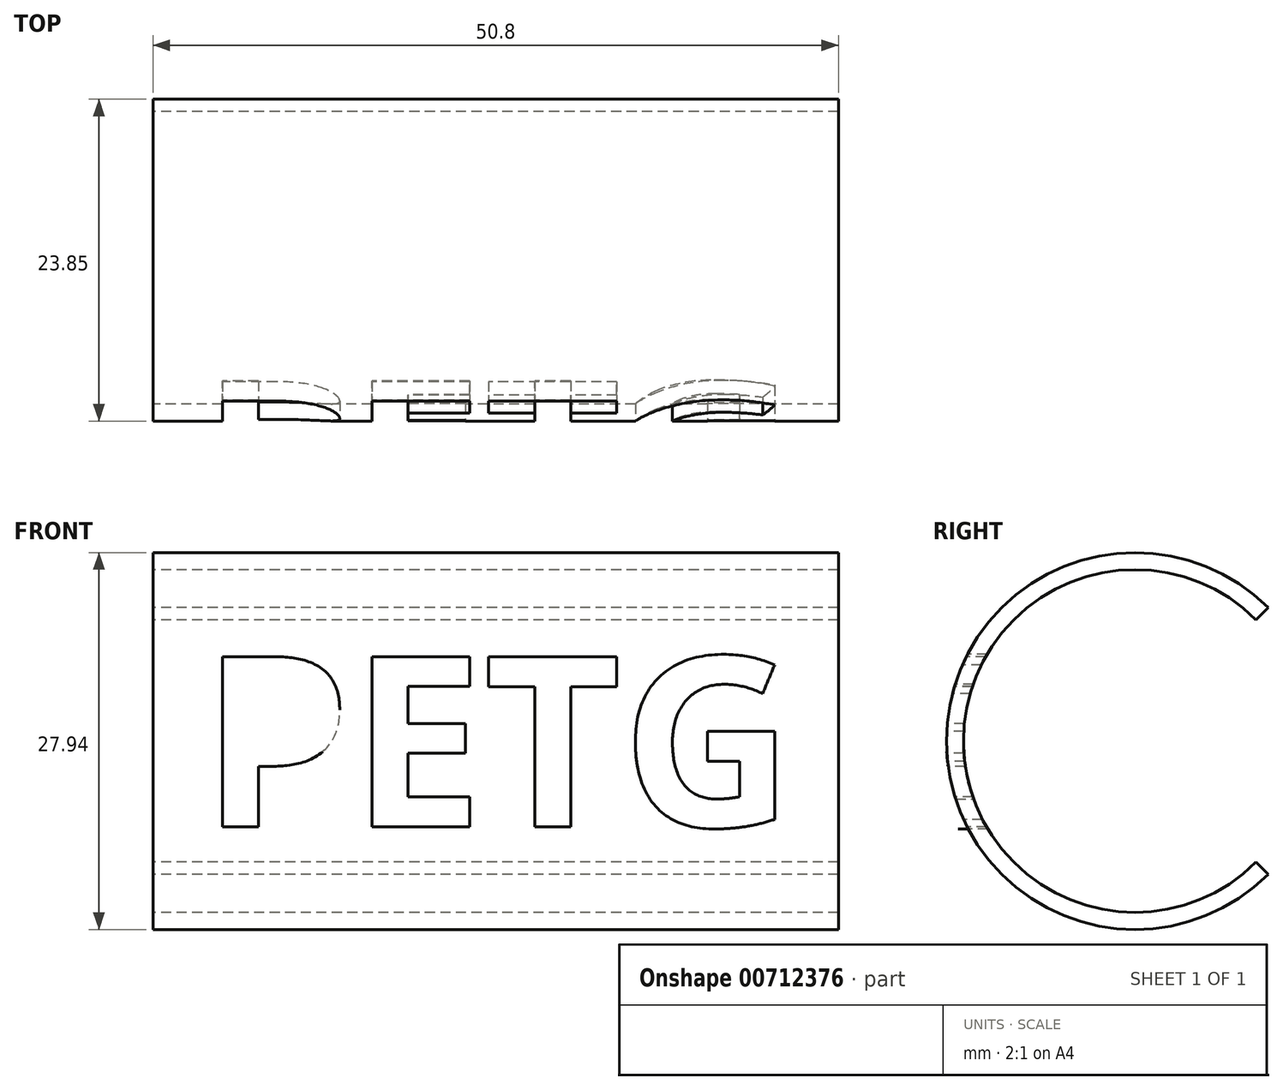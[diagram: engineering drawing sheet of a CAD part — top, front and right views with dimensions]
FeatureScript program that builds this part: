
annotation { "Feature Type Name" : "Feature", "Feature Type Description" : "" }
export const myFeature = defineFeature(function(context is Context, id is Id, definition is map)
    precondition{}
    {
        {
            var Q0;
            Q0=qCreatedBy(makeId("Right.planeOp"),FACE);
            var sketch = newSketch(context, id + "F0", { "sketchPlane" : qUnion([Q0])});
            skCircle(sketch, "E0", {"center": v(0, 0) * mm, "radius": 12.7 * mm});
            skCircle(sketch, "E1", {"center": v(0, 0) * mm, "radius": 13.97 * mm});
            skLineSegment(sketch, "E2", {"start": v(0, 0) * mm, "end": v(13.97, 0) * mm});
            skLineSegment(sketch, "E3", {"start": v(0, 0) * mm, "end": v(9.88, 9.88) * mm});
            skLineSegment(sketch, "E4.MirrorCS", {"start": v(0, 0) * mm, "end": v(9.88, -9.88) * mm});
            skSolve(sketch);
        }
        {
            var Q0;
            {var subQ0=sQuery(id+"F0.wireOp",EDGE,"E3");var subQ1=sQuery(id+"F0.wireOp",EDGE,"E0");var subQ2=makeQuery(id+"F0.imprint","INTERSECT",VERTEX,{"derivedFrom":[subQ1,subQ0]});Q0=makeQuery(id+"F0.imprint","IMPRINT",FACE,{"disambiguationData":[TD([[makeQuery(id+"F0.imprint","IMPRINT",EDGE,{"disambiguationData":[TD([[subQ2,-1.0]])],"derivedFrom":subQ1}),-1.0]])]});}
            extrude(context, id + "F1", {"entities" : qUnion([Q0]), "depth" : 50.8 * mm, "offsetDistance" : 25.4 * mm});
        }
        {
            var Q0;
            Q0=qCreatedBy(makeId("Front.planeOp"),FACE);
            cPlane(context, id + "F2", {"entities" : qUnion([Q0]), "cplaneType" : CPlaneType.OFFSET, "offset" : 25.4 * mm, "width" : 152.4 * mm, "height" : 152.4 * mm});
        }
        {
            var Q0;
            Q0=qCreatedBy(id+"F2.planeOp",FACE);
            var sketch = newSketch(context, id + "F3", { "sketchPlane" : qUnion([Q0])});
            skLineSegment(sketch, "E5.bottom", {"start": v(0, 13.97) * mm, "end": v(50.8, 13.97) * mm});
            skLineSegment(sketch, "E5.top", {"start": v(0, -13.97) * mm, "end": v(50.8, -13.97) * mm});
            skLineSegment(sketch, "E5.left", {"start": v(0, 13.97) * mm, "end": v(0, -13.97) * mm});
            skLineSegment(sketch, "E5.right", {"start": v(50.8, 13.97) * mm, "end": v(50.8, -13.97) * mm});
            skPoint(sketch, "E6", {"position": v(25.4, 13.97) * mm});
            skPoint(sketch, "E7", {"position": v(3.96, 0) * mm});
            skText(sketch, "E8", { "text": "PETG", "fontName": "OpenSans-Bold.ttf"});
            const initialGuessF3  = {"E8": [0.00356, -0.00635, 1, 0, 0.0127]};
            skSetInitialGuess(sketch, initialGuessF3);
            skSolve(sketch);
        }
        {
            var Q0;
            Q0=makeQuery(id+"F3.imprint","IMPRINT",FACE,{"disambiguationData":[TD([[makeQuery(id+"F3.imprint","IMPRINT",EDGE,{"derivedFrom":sQuery(id+"F3.wireOp",EDGE,"E8.sketch_text.stroke-0")}),-1.0]])]});
            var Q1;
            Q1=makeQuery(id+"F3.imprint","IMPRINT",FACE,{"disambiguationData":[TD([[makeQuery(id+"F3.imprint","IMPRINT",EDGE,{"derivedFrom":sQuery(id+"F3.wireOp",EDGE,"E8.sketch_text.stroke-16")}),-1.0]])]});
            var Q2;
            Q2=makeQuery(id+"F3.imprint","IMPRINT",FACE,{"disambiguationData":[TD([[makeQuery(id+"F3.imprint","IMPRINT",EDGE,{"derivedFrom":sQuery(id+"F3.wireOp",EDGE,"E8.sketch_text.stroke-28")}),-1.0]])]});
            var Q3;
            Q3=makeQuery(id+"F3.imprint","IMPRINT",FACE,{"disambiguationData":[TD([[makeQuery(id+"F3.imprint","IMPRINT",EDGE,{"derivedFrom":sQuery(id+"F3.wireOp",EDGE,"E8.sketch_text.stroke-36")}),-1.0]])]});
            var Q4;
            Q4=makeQuery(id+"F3.imprint","IMPRINT",FACE,{"disambiguationData":[TD([[makeQuery(id+"F3.imprint","IMPRINT",EDGE,{"derivedFrom":sQuery(id+"F3.wireOp",EDGE,"E8.sketch_text.stroke-0")}),1.0]])]});
            extrude(context, id + "F4", {"entities" : qUnion([Q0, Q1, Q2, Q3, Q4]), "operationType" : NewBodyOperationType.REMOVE, "endBound" : BoundingType.THROUGH_ALL, "oppositeDirection" : true, "depth" : 25.4 * mm, "offsetDistance" : 25.4 * mm});
        }
    });
